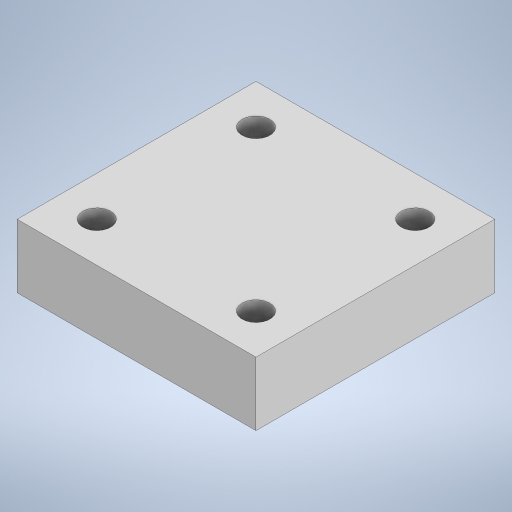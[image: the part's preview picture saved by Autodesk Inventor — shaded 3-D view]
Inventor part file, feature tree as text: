
AUTODESK INVENTOR PART (.ipt)
format: ipt  version: 2023 (Build 270158000, 158)  size: 204,800 bytes
history: native  units: mm
features: other x1, extrude x1, sketch x1
ambient origin geometry x8: Origin, YZ Plane, XZ Plane, XY Plane, X Axis, Y Axis, Z Axis, Center Point
bodies: Body1 (feature_tree)
feature tree (3):
  other  "Sólido1"
  extrude  "Extrusión1"  Depth=30.0mm
  sketch  "Boceto1"  dims[d0=30.0mm d1=30.0mm d2=3.5mm d3=10.0mm d4=10.0mm d5=8.0mm d6=0.0mm]
